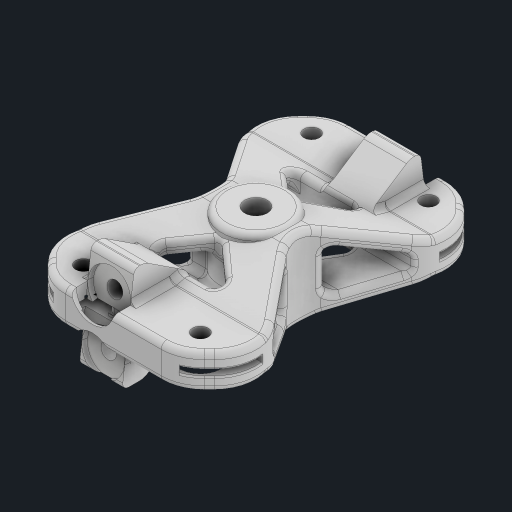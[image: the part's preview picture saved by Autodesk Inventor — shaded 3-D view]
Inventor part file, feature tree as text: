
AUTODESK INVENTOR PART (.ipt)
format: ipt  version: 2023 (Build 270158000, 158)  size: 2,088,960 bytes
history: native  units: mm
features: extrude x26, fillet x22, sketch x9, chamfer x6, mirror x2, plane x1, loft x1, other x1
ambient origin geometry x8: Origin, YZ Plane, XZ Plane, XY Plane, X Axis, Y Axis, Z Axis, Center Point
bodies: Body1 (feature_tree)
feature tree (68):
  sketch  "Sketch1"  dims[d13=261.822mm d14=7.45mm]
  plane  "Work Plane1"
  sketch  "Sketch2"  dims[d15=27.223mm d17=1.0mm]
  extrude  "Extrusion26"  Depth=7.45mm
  extrude  "Extrusion27"  Depth=1.0mm
  loft  "Loft4"
  extrude  "Extrusion30"  Depth=1.0mm
  chamfer  "Chamfer7"  Distance=15.0mm
  chamfer  "Chamfer8"  Distance=1.0mm
  extrude  "Extrusion45"  Depth=0.5mm
  extrude  "Extrusion55"  Depth=0.5mm TaperAngle=0.0deg
  extrude  "Extrusion57"  Depth=0.5mm
  sketch  "Sketch19"  dims[d26=90.0deg]
  extrude  "Extrusion67"  Depth=0.5mm
  extrude  "Extrusion68"  Depth=0.5mm TaperAngle=0.0deg
  mirror  "Mirror6"
  extrude  "Extrusion69"  Depth=0.5mm TaperAngle=0.0deg
  chamfer  "Chamfer18"  Distance=19.96mm
  chamfer  "Chamfer19"  Angle=90.0deg  [1 undecoded]
  chamfer  "Chamfer20"  Angle=90.0deg  [1 undecoded]
  chamfer  "Chamfer21"  Distance=2.0mm
  sketch  "Sketch23"  dims[d28=90.0deg d29=5.5mm d30=15.0mm]
  extrude  "Extrusion71"  Depth=2.0mm
  extrude  "Extrusion72"  Depth=0.5mm TaperAngle=45.0deg
  fillet  "Fillet54"  Radius=12.0mm
  extrude  "Extrusion73"  Depth=15.0mm
  sketch  "Sketch24"  dims[d31=65.0mm]
  extrude  "Extrusion74"  Depth=0.5mm TaperAngle=0.0deg
  extrude  "Extrusion75"  Depth=0.5mm
  extrude  "Extrusion76"  Depth=0.5mm
  fillet  "Fillet55"  Radius=10.0mm
  fillet  "Fillet56"  Radius=100.0mm
  extrude  "Extrusion77"  Depth=0.5mm
  fillet  "Fillet58"  Radius=5.0mm
  extrude  "Extrusion78"  Depth=0.5mm
  extrude  "Extrusion79"  Depth=0.5mm
  fillet  "Fillet59"  Radius=100.0mm
  fillet  "Fillet60"  Radius=35.0mm
  fillet  "Fillet61"  Radius=5.0mm
  fillet  "Fillet62"  Radius=5.0mm
  fillet  "Fillet64"  Radius=0.25mm
  fillet  "Fillet65"  Radius=15.0mm
  fillet  "Fillet66"  Radius=15.0mm
  fillet  "Fillet67"  Radius=30.0mm
  fillet  "Fillet68"  Radius=15.0mm
  fillet  "Fillet69"  Radius=30.0mm
  fillet  "Fillet70"  Radius=14.0mm
  fillet  "Fillet71"  Radius=14.0mm
  extrude  "Extrusion80"  Depth=0.5mm TaperAngle=45.0deg
  extrude  "Extrusion81"  Depth=0.5mm TaperAngle=45.0deg
  extrude  "Extrusion82"  Depth=15.0mm
  extrude  "Extrusion83"  Depth=15.0mm
  extrude  "Extrusion84"  Depth=15.0mm
  fillet  "Fillet72"  Radius=2.5mm
  mirror  "Mirror7"
  fillet  "Fillet73"  Radius=15.0mm
  fillet  "Fillet74"  Radius=15.0mm
  fillet  "Fillet75"  Radius=15.0mm
  fillet  "Fillet76"  Radius=15.0mm
  fillet  "Fillet77"  [1 undecoded]
  extrude  "Extrusion85"  Depth=15.0mm
  extrude  "Extrusion86"  Depth=0.5mm
  extrude  "Extrusion87"  Depth=15.0mm
  sketch  "Sketch12"  dims[d21=35.0mm d22=100.0mm]
  other  "Edges5"
  sketch  "Sketch18"  dims[d23=2.0mm d25=1.0mm]
  sketch  "Sketch21"  dims[d27=1.0mm]
  sketch  "Sketch25"  dims[d56=12.0mm d74=1.0mm d75=8.0mm d148=244.423mm d149=41.005864mm d150=244.423mm d151=5.5mm d152=5.5mm d153=5.5mm d154=15.0mm d155=15.0mm d156=18.0mm d157=5.5mm d158=160.0mm d159=7.0mm d160=0.0mm d161=8.0mm d162=24.0mm d163=30.0mm d164=0.0mm d165=5.0mm d166=0.0mm d167=19.96mm d170=0.0mm d171=90.0deg d172=0.0mm d173=90.0deg d178=2.0mm d179=0.0mm d180=2.0mm d206=12.0mm d207=12.0mm d208=45.0deg d209=12.0mm d210=12.0mm d211=45.0deg d256=15.0mm d257=30.0mm d258=0.0mm d271=14.0mm d272=100.0mm d273=10.0mm d274=100.0mm d313=5.5mm d316=5.0mm d317=5.0mm d318=16.0mm d319=100.0mm d320=0.0mm d324=35.0mm d325=0.0mm d333=5.0mm d341=5.0mm d369=0.25mm d370=0.0mm d379=15.0mm d380=0.0mm d381=15.0mm d382=0.0mm d386=30.0mm d392=15.0mm d394=30.0mm d395=0.0mm d396=14.0mm d397=9.1686mm d398=45.0deg d399=14.0mm d400=9.1686mm d401=45.0deg d402=10.83mm d403=14.0mm d404=45.0deg d405=10.9mm d406=14.0mm d407=45.0deg d418=15.0mm d419=15.0mm d420=15.0mm d421=2.5mm d422=15.0mm d423=15.0mm d424=15.0mm d425=15.0mm d426=90.0deg d427=15.0mm d428=5.5mm d429=15.0mm d430=5.5mm d435=18.0mm d436=0.0mm d437=15.0mm d438=0.0mm d439=2.0mm d440=15.0mm d441=2.0mm d442=0.0mm d443=0.0mm d444=15.0mm d445=15.0mm d446=15.0mm d447=2.5mm d448=15.0mm d449=15.0mm d450=15.0mm d451=90.0deg d452=15.0mm d453=90.0deg d454=15.0mm d455=5.5mm d456=15.0mm d457=5.5mm d458=15.0mm d459=2.0mm d460=0.0mm d461=0.0mm d462=18.0mm d463=0.0mm d464=15.0mm d465=0.0mm d466=10.0mm d467=15.0mm d469=20.0mm d470=1.0mm d471=30.0mm d472=0.0mm d473=2.0mm d474=20.0mm d475=0.0mm d476=35.0mm d477=0.0mm d478=20.0mm d479=2.0mm d480=2.0mm d481=2.0mm d483=2.0mm d484=2.0mm d485=2.0mm d486=2.0mm d487=2.0mm d488=2.0mm d489=2.0mm d490=2.0mm d491=10.0mm d492=0.0mm d493=10.0mm d494=0.0mm d495=3.0mm d496=0.0mm d498=90.0deg d499=10.0mm d500=0.0mm d501=2.0mm d502=0.0mm d503=2.0mm d504=5.0mm d505=2.0mm d506=2.0mm d507=2.0mm d508=0.5mm d509=1.218294mm d510=15.0mm d511=0.0mm d512=15.0mm d513=0.0mm d514=2.0mm d515=2.0mm d516=15.0mm d517=0.0mm d76=0.5mm d77=0.872665mm d144=0.5mm d145=0.872665mm d146=0.5mm d147=0.872665mm d241=0.0mm d242=0.0mm d243=0.0mm d244=0.0mm d268=0.0mm d269=0.0mm d270=0.0mm d342=0.872665mm d343=0.5mm d344=0.872665mm d348=0.0mm d349=0.0mm d350=0.0mm d351=0.0mm d352=0.0mm d353=0.0mm d354=0.0mm d357=0.0mm d358=0.0mm d359=0.0mm d360=0.0mm]
note: 3 required parameter values undecoded (feature->parameter linkage not recoverable at this tier; creation-order binding heuristic only, values carry confidence <= 0.55)
